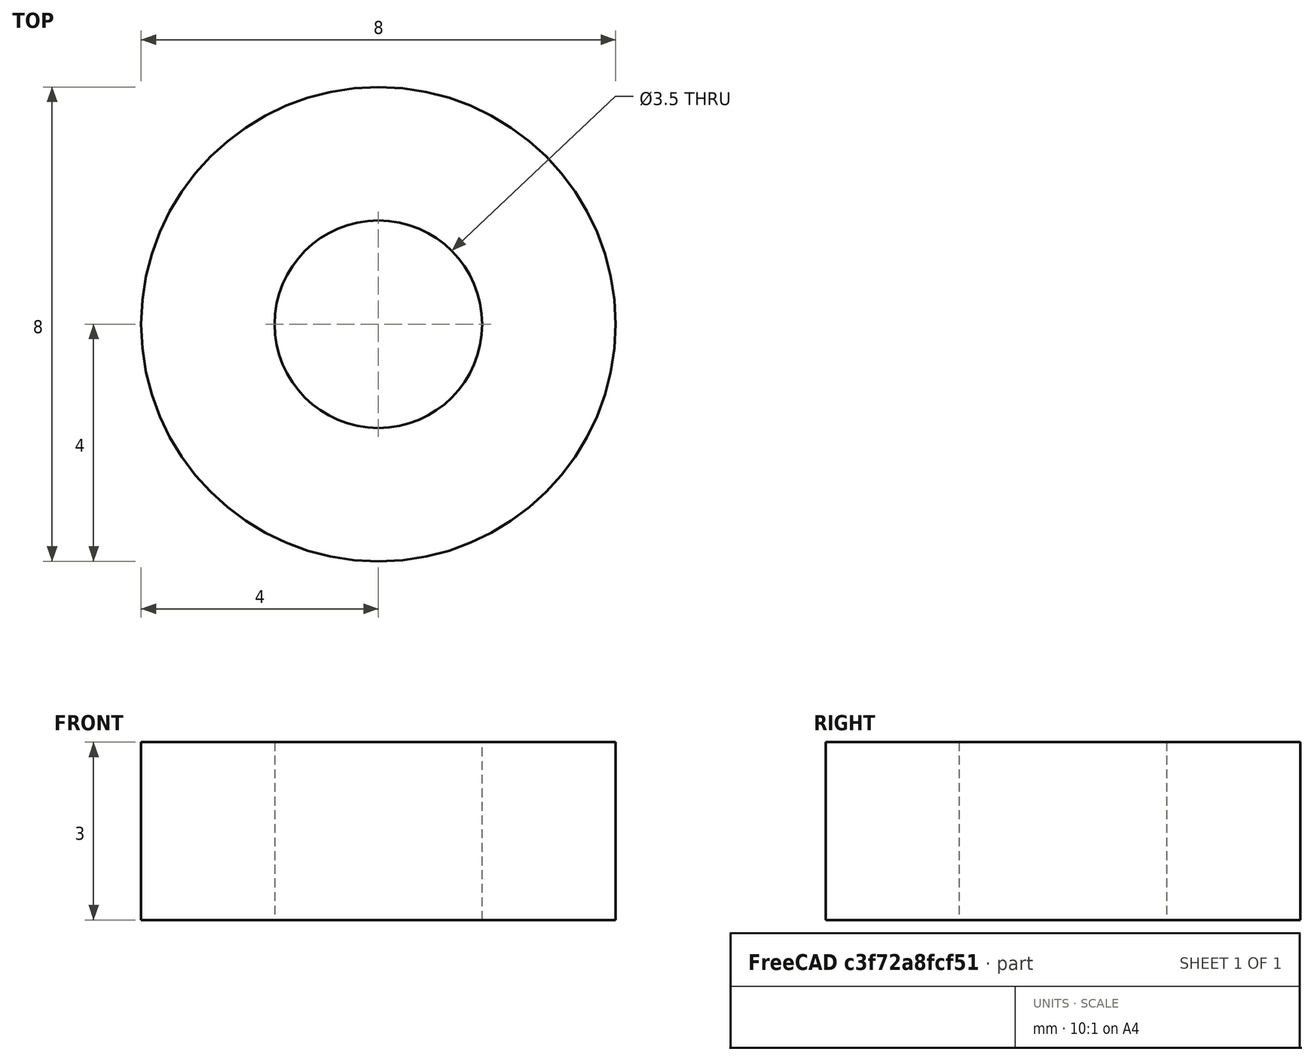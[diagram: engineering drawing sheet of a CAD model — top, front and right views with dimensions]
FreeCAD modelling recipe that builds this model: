
FCSTD DOCUMENT  (FreeCAD 0.19R24267 +148 (Git))
Label: distance
License: All rights reserved
LicenseURL: http://en.wikipedia.org/wiki/All_rights_reserved
objects: Sketcher::SketchObject×1, PartDesign::Pad×1, PartDesign::Body×1
note: 4 computed .brp shape members not serialized (recipe doc carries the construction recipe); baked Part::Feature solids carry a one-line shape summary decoded from their .brp

FEATURE [Sketcher::SketchObject] Sketch
  FullyConstrained = true
  MapMode = 5
  Support = -> [XY_Plane]
  sketch-geometry (2):
    g0: Circle CenterX=0 CenterY=0 CenterZ=0 NormalX=0 NormalY=0 NormalZ=1 AngleXU=0 Radius=4
    g1: Circle CenterX=0 CenterY=0 CenterZ=0 NormalX=0 NormalY=0 NormalZ=1 AngleXU=0 Radius=1.75
  constraints (4):
    c: Coincident(g0,g-1)
    c: Coincident(g1,g0)
    c: Radius(g0) = 4
    c: Radius(g1) = 1.75
FEATURE [PartDesign::Pad] Pad
  Direction = (1,1,1)
  Length = 3
  Length2 = 100
  Profile = -> Sketch
  Type = 0
FEATURE [PartDesign::Body] Body
  Group = -> [Sketch,Pad]
  Origin = -> Origin
  Tip = -> Pad
